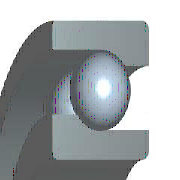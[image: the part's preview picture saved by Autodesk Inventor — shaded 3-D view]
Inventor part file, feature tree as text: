
AUTODESK INVENTOR PART (.ipt)
format: ipt  version: 2025 (Build 290162010, 162A)  size: 292,864 bytes
history: native  units: mm (DEFAULTED — no unit token found)
features: sketch x6, other x5, plane x3, fillet x2, pattern_circular x1
ambient origin geometry x8: Origin, YZ Plane, XZ Plane, XY Plane, X Axis, Y Axis, Z Axis, Center Point
bodies: Solid1 (feature_tree)
feature tree (17):
  plane  "WorkPlane1"
  plane  "Work Plane2"
  plane  "WorkPlane2"
  sketch  "Sketch1"  dims[d0=-15.0mm]
  other  "WorkPoint1"
  sketch  "Sketch2"  dims[d1=10.0mm]
  other  "WorkPoint3"
  sketch  "Sketch3"  dims[d2=12.5mm]
  other  "WorkPoint2"
  other  "WorkAxis1"
  other  "Work Axis2"
  pattern_circular  "PolarArray1"  [2 undecoded]
  fillet  "Fillet1"  [1 undecoded]
  fillet  "Fillet2"  Radius=7.0mm
  sketch  "Sketch4"  dims[d3=23.5mm]
  sketch  "Sketch5"  dims[d4=26.0mm]
  sketch  "Sketch6"  dims[d5=14.0mm d6=15.0mm d7=360.0deg d8=7.0mm d9=7.5mm d10=8.1mm d11=8.1mm d12=360.0deg d13=4.05mm d14=4.05mm d15=360.0deg d16=70.0mm d18=360.0deg d19=0.6mm d20=1.0mm d21=38.5mm d22=33.64mm d23=43.36mm d26=0.0mm d27=0.0mm d28=0.0mm d29=0.0mm d30=0.0mm]
note: 3 required parameter values undecoded (feature->parameter linkage not recoverable at this tier; creation-order binding heuristic only, values carry confidence <= 0.55)
